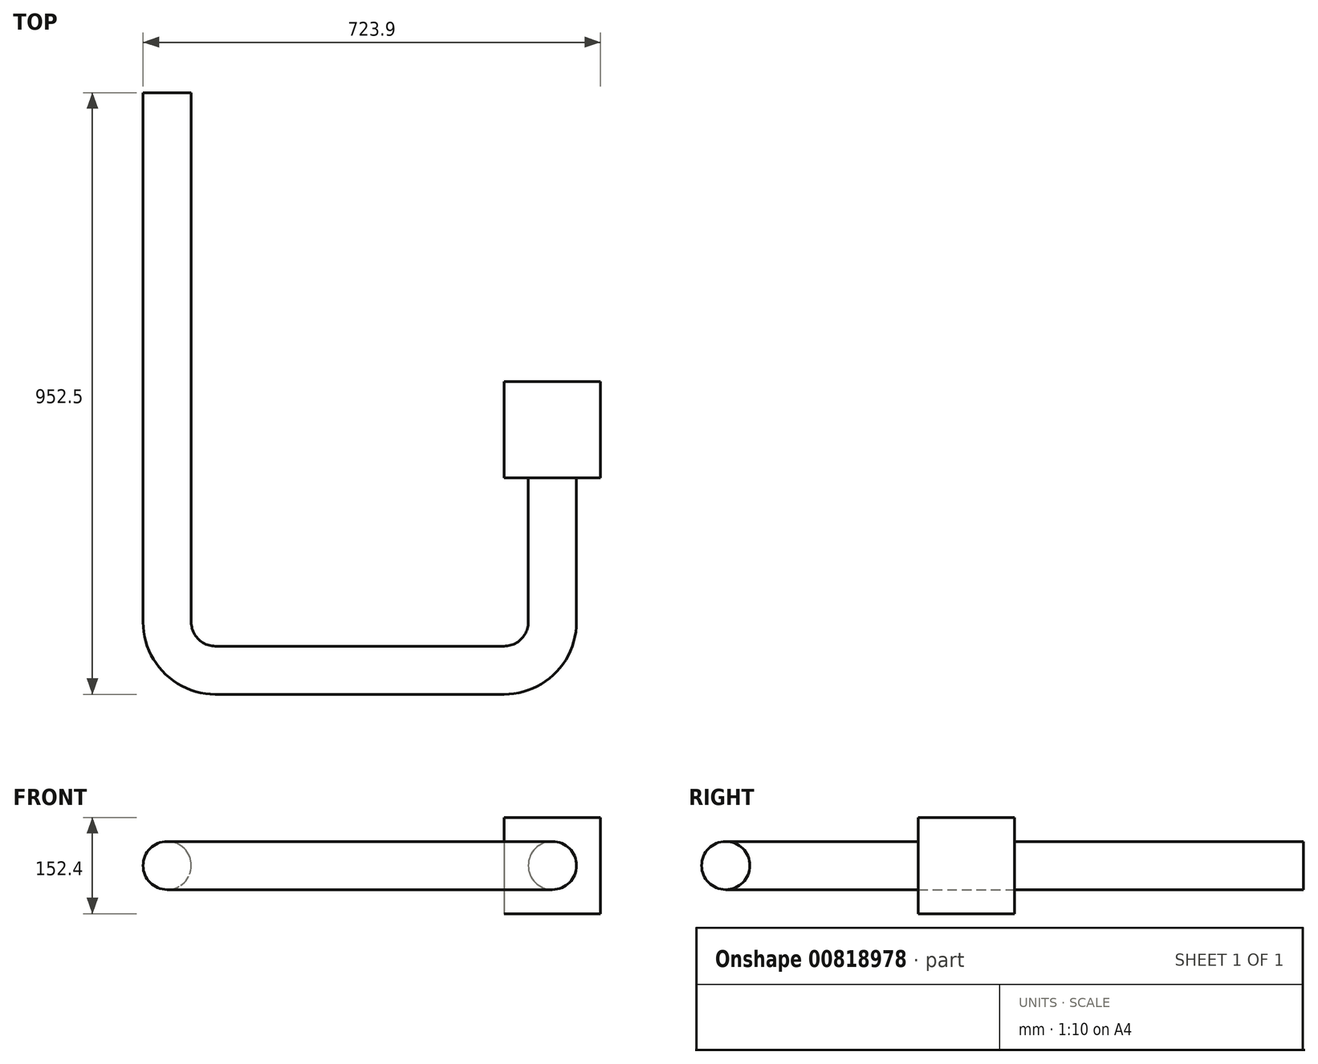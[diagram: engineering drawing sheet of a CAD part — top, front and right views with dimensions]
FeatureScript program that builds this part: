
annotation { "Feature Type Name" : "Feature", "Feature Type Description" : "" }
export const myFeature = defineFeature(function(context is Context, id is Id, definition is map)
    precondition{}
    {
        {
            var Q0;
            Q0=qCreatedBy(makeId("Top.planeOp"),FACE);
            var sketch = newSketch(context, id + "F0", { "sketchPlane" : qUnion([Q0])});
            skLineSegment(sketch, "E0", {"start": v(0, 0) * mm, "end": v(0, -228.6) * mm});
            skLineSegment(sketch, "E1", {"start": v(-76.2, -304.8) * mm, "end": v(-533.4, -304.8) * mm});
            skLineSegment(sketch, "E2", {"start": v(-609.6, -228.6) * mm, "end": v(-609.6, 609.6) * mm});
            skPoint(sketch, "E3.visualSharp", {"position": v(-609.6, -304.8) * mm});
            skArc(sketch, "E3.filletArc", {"start": v(-609.6, -228.6) * mm, "mid": v(-587.28, -282.48) * mm, "end": v(-533.4, -304.8) * mm});
            skPoint(sketch, "E4.visualSharp", {"position": v(0, -304.8) * mm});
            skArc(sketch, "E4.filletArc", {"start": v(-76.2, -304.8) * mm, "mid": v(-22.32, -282.48) * mm, "end": v(0, -228.6) * mm});
            skSolve(sketch);
        }
        {
            var Q0;
            Q0=qCreatedBy(makeId("Front.planeOp"),FACE);
            var sketch = newSketch(context, id + "F1", { "sketchPlane" : qUnion([Q0])});
            skCircle(sketch, "E5", {"center": v(0, 0) * mm, "radius": 38.1 * mm});
            skSolve(sketch);
        }
        {
            var Q0;
            Q0=makeQuery(id+"F1.imprint","IMPRINT",FACE,{"disambiguationData":[TD([[makeQuery(id+"F1.imprint","IMPRINT",EDGE,{"derivedFrom":sQuery(id+"F1.wireOp",EDGE,"E5")}),1.0]])]});
            var Q1;
            Q1=sQuery(id+"F0.wireOp",EDGE,"E0");
            var Q2;
            Q2=sQuery(id+"F0.wireOp",EDGE,"E4.filletArc");
            var Q3;
            Q3=sQuery(id+"F0.wireOp",EDGE,"E1");
            var Q4;
            Q4=sQuery(id+"F0.wireOp",EDGE,"E3.filletArc");
            var Q5;
            Q5=sQuery(id+"F0.wireOp",EDGE,"E2");
            sweep(context, id + "F2", {"profiles" : qUnion([Q0]), "path" : qUnion([Q1, Q2, Q3, Q4, Q5])});
        }
        {
            var Q0;
            Q0=qCreatedBy(makeId("Front.planeOp"),FACE);
            var sketch = newSketch(context, id + "F3", { "sketchPlane" : qUnion([Q0])});
            skLineSegment(sketch, "E6.bottom", {"start": v(76.2, 76.2) * mm, "end": v(-76.2, 76.2) * mm});
            skLineSegment(sketch, "E6.top", {"start": v(76.2, -76.2) * mm, "end": v(-76.2, -76.2) * mm});
            skLineSegment(sketch, "E6.left", {"start": v(76.2, 76.2) * mm, "end": v(76.2, -76.2) * mm});
            skLineSegment(sketch, "E6.right", {"start": v(-76.2, 76.2) * mm, "end": v(-76.2, -76.2) * mm});
            skLineSegment(sketch, "E7", {"start": v(0, 76.2) * mm, "end": v(0, -76.2) * mm, "construction": true});
            skSolve(sketch);
        }
        {
            var Q0;
            Q0=makeQuery(id+"F3.imprint","IMPRINT",FACE,{"disambiguationData":[TD([[makeQuery(id+"F3.imprint","IMPRINT",EDGE,{"derivedFrom":sQuery(id+"F3.wireOp",EDGE,"E6.bottom")}),1.0]])]});
            extrude(context, id + "F4", {"entities" : qUnion([Q0]), "oppositeDirection" : true, "depth" : 152.4 * mm, "offsetDistance" : 25.4 * mm});
        }
    });
